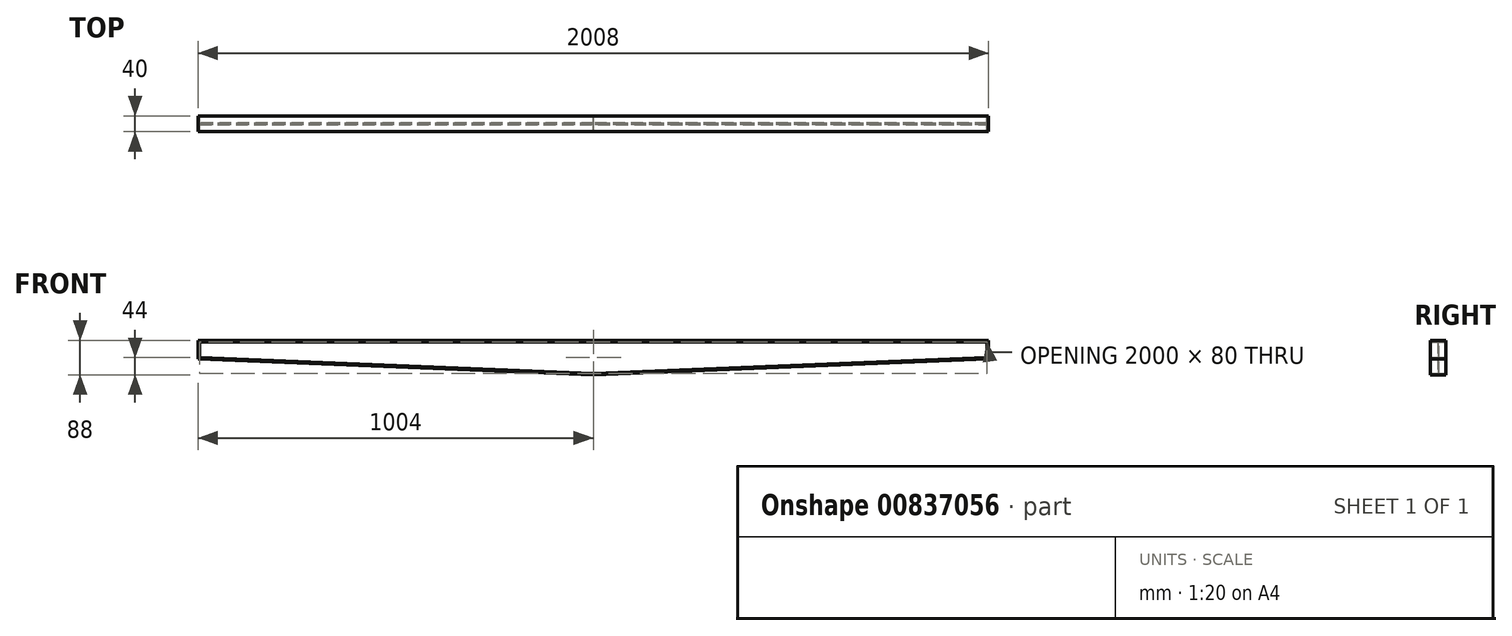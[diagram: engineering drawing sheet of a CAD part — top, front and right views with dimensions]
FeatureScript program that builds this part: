
annotation { "Feature Type Name" : "Feature", "Feature Type Description" : "" }
export const myFeature = defineFeature(function(context is Context, id is Id, definition is map)
    precondition{}
    {
        {
            var Q0;
            Q0=qCreatedBy(makeId("Front.planeOp"),FACE);
            var sketch = newSketch(context, id + "F0", { "sketchPlane" : qUnion([Q0])});
            skLineSegment(sketch, "E0", {"start": v(0, 40) * mm, "end": v(1000, 40) * mm});
            skLineSegment(sketch, "E1", {"start": v(1000, 40) * mm, "end": v(1000, 0) * mm});
            skLineSegment(sketch, "E2", {"start": v(1000, 0) * mm, "end": v(0, -40) * mm});
            skLineSegment(sketch, "E3", {"start": v(0, -40) * mm, "end": v(-1000, 0) * mm});
            skLineSegment(sketch, "E4", {"start": v(-1000, 0) * mm, "end": v(-1000, 40) * mm});
            skLineSegment(sketch, "E5", {"start": v(-1000, 40) * mm, "end": v(0, 40) * mm});
            skSolve(sketch);
        }
        {
            var Q0;
            Q0 = qSketchRegion(id + "F0", true);
            extrude(context, id + "F1", {"entities" : qUnion([Q0]), "depth" : 3 * mm, "offsetDistance" : 25 * mm, "symmetric" : true});
        }
        {
            var Q0;
            Q0=qCreatedBy(makeId("Front.planeOp"),FACE);
            var sketch = newSketch(context, id + "F2", { "sketchPlane" : qUnion([Q0])});
            skLineSegment(sketch, "E6", {"start": v(1000, 40) * mm, "end": v(-1000, 40) * mm});
            skLineSegment(sketch, "E7", {"start": v(-1000, 40) * mm, "end": v(-1000, 0) * mm});
            skLineSegment(sketch, "E8", {"start": v(-1000, 0) * mm, "end": v(0, -40) * mm});
            skLineSegment(sketch, "E9", {"start": v(0, -40) * mm, "end": v(1000, 0) * mm});
            skLineSegment(sketch, "E10", {"start": v(1000, 0) * mm, "end": v(1000, 40) * mm});
            skLineSegment(sketch, "E11", {"start": v(1004, 44) * mm, "end": v(-1004, 44) * mm});
            skLineSegment(sketch, "E12", {"start": v(-1004, 44) * mm, "end": v(-1004, -3.84) * mm});
            skLineSegment(sketch, "E13", {"start": v(-1004, -3.84) * mm, "end": v(0, -44) * mm});
            skLineSegment(sketch, "E14", {"start": v(0, -44) * mm, "end": v(1004, -3.84) * mm});
            skLineSegment(sketch, "E15", {"start": v(1004, -3.84) * mm, "end": v(1004, 44) * mm});
            skSolve(sketch);
        }
        {
            var Q0;
            Q0 = qSketchRegion(id + "F2", true);
            extrude(context, id + "F3", {"entities" : qUnion([Q0]), "operationType" : NewBodyOperationType.ADD, "depth" : 40 * mm, "offsetDistance" : 25 * mm, "symmetric" : true});
        }
    });
